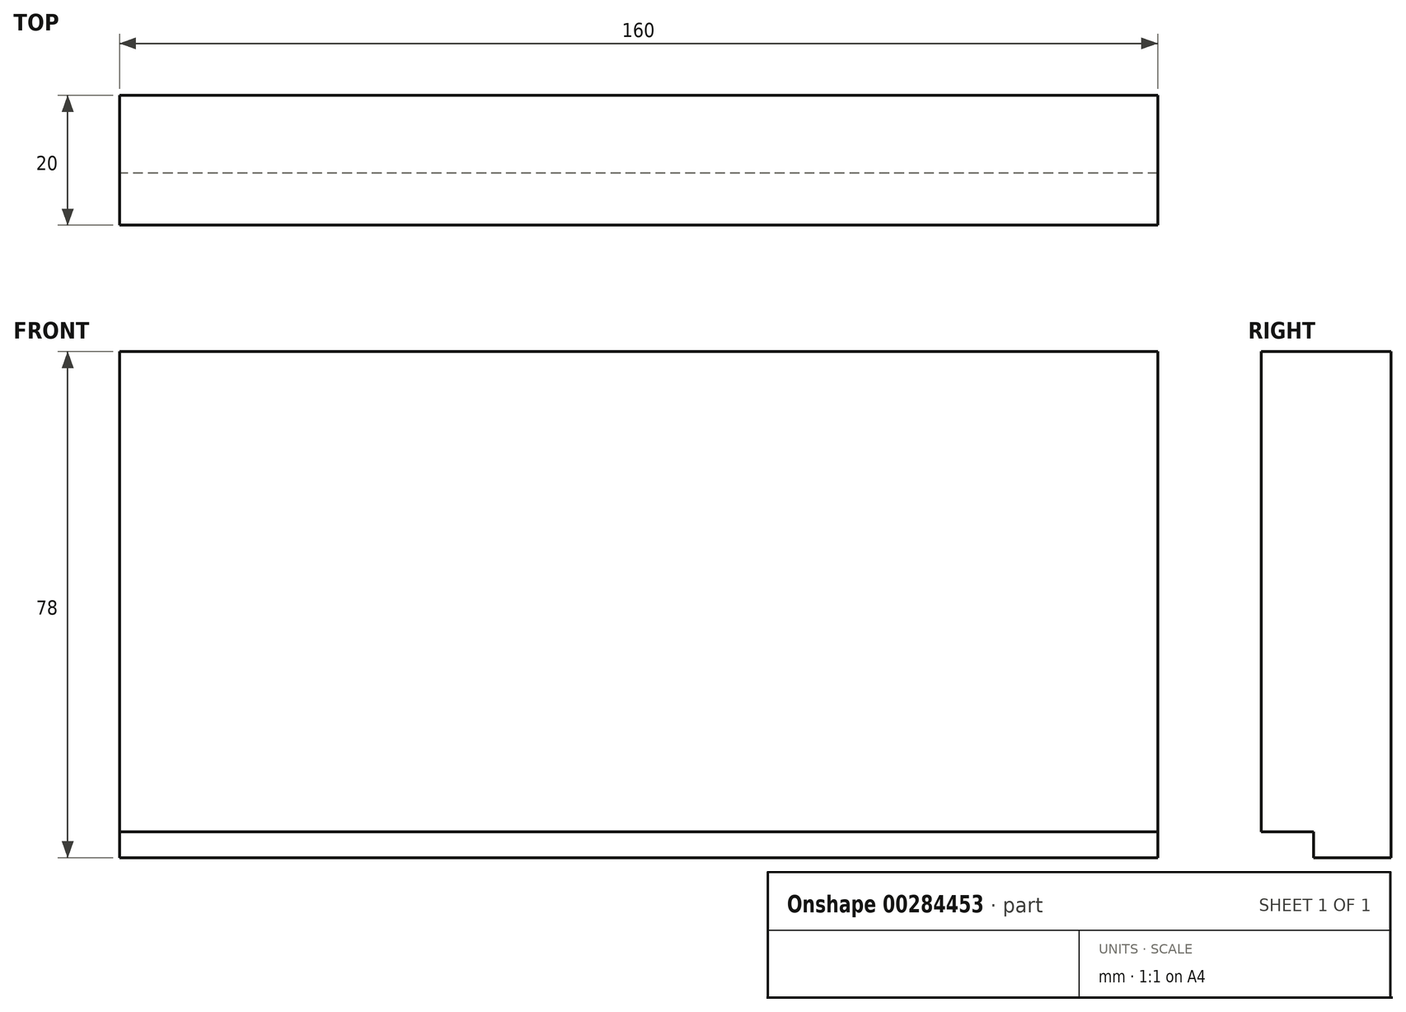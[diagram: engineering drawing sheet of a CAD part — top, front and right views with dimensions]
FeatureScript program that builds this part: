
annotation { "Feature Type Name" : "Feature", "Feature Type Description" : "" }
export const myFeature = defineFeature(function(context is Context, id is Id, definition is map)
    precondition{}
    {
        {
            var Q0;
            Q0=qCreatedBy(makeId("Front.planeOp"),FACE);
            var sketch = newSketch(context, id + "F0", { "sketchPlane" : qUnion([Q0])});
            skLineSegment(sketch, "E0.bottom", {"start": v(80, -39) * mm, "end": v(-80, -39) * mm});
            skLineSegment(sketch, "E0.top", {"start": v(80, 39) * mm, "end": v(-80, 39) * mm});
            skLineSegment(sketch, "E0.left", {"start": v(80, -39) * mm, "end": v(80, 39) * mm});
            skLineSegment(sketch, "E0.right", {"start": v(-80, -39) * mm, "end": v(-80, 39) * mm});
            skPoint(sketch, "E0.middle", {"position": v(0, 0) * mm});
            skLineSegment(sketch, "E1", {"start": v(-80, -35) * mm, "end": v(80, -35) * mm});
            skSolve(sketch);
        }
        {
            var Q0;
            {var subQ0=sQuery(id+"F0.wireOp",EDGE,"E0.bottom");Q0=makeQuery(id+"F0.imprint","IMPRINT",FACE,{"disambiguationData":[TD([[makeQuery(id+"F0.imprint","IMPRINT",EDGE,{"derivedFrom":subQ0}),-1.0]])]});}
            extrude(context, id + "F1", {"entities" : qUnion([Q0]), "depth" : 12 * mm});
        }
        {
            var Q0;
            {var subQ0=sQuery(id+"F0.wireOp",EDGE,"E0.top");Q0=makeQuery(id+"F0.imprint","IMPRINT",FACE,{"disambiguationData":[TD([[makeQuery(id+"F0.imprint","IMPRINT",EDGE,{"derivedFrom":subQ0}),1.0]])]});}
            extrude(context, id + "F2", {"entities" : qUnion([Q0]), "operationType" : NewBodyOperationType.ADD, "depth" : 20 * mm});
        }
    });
